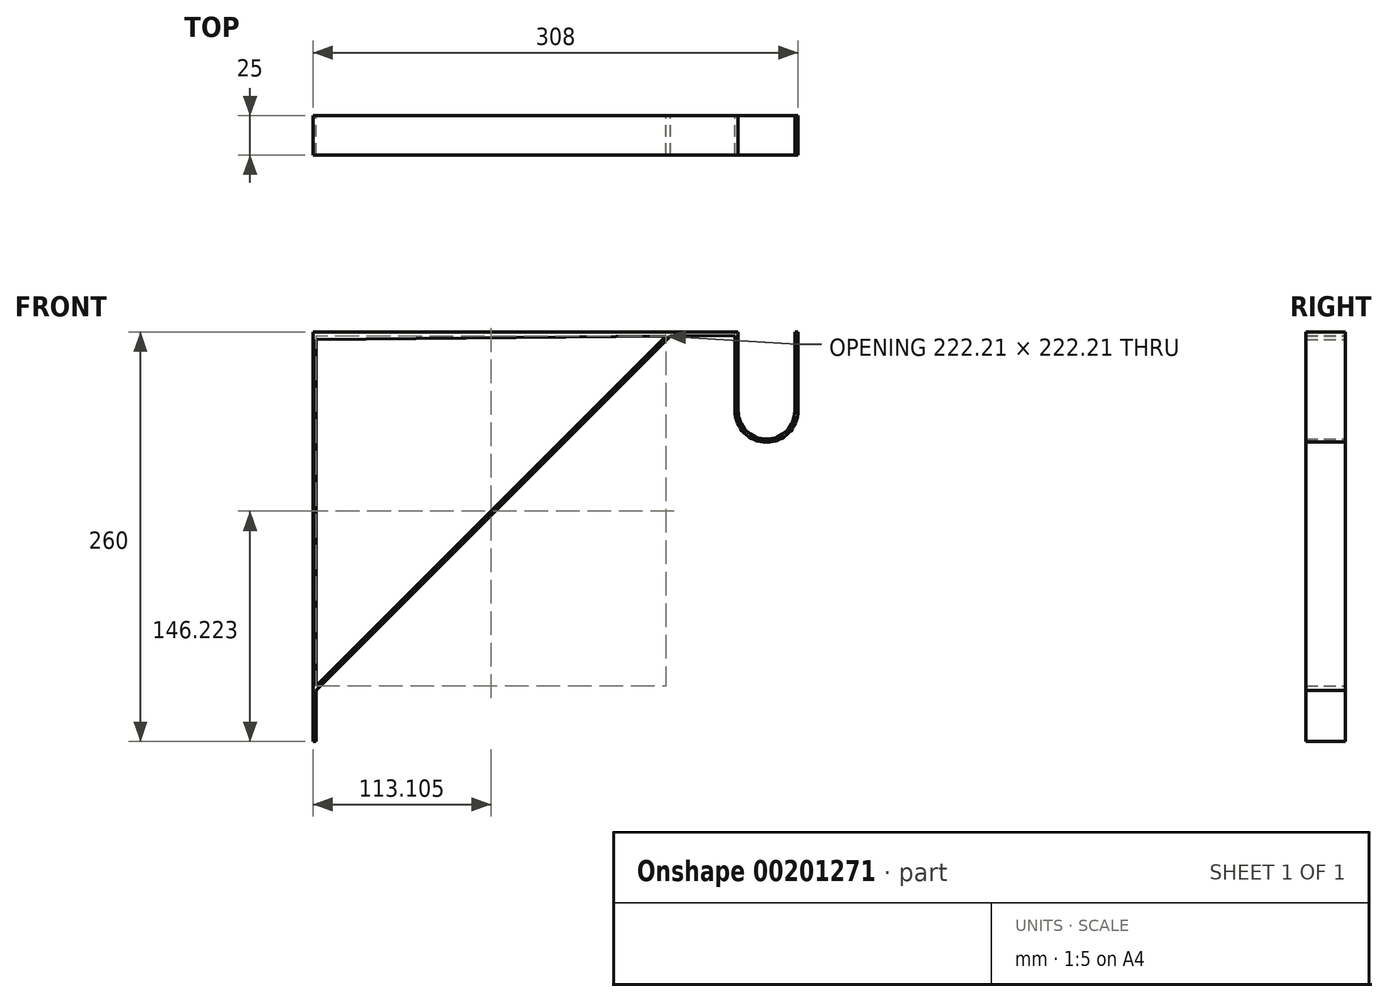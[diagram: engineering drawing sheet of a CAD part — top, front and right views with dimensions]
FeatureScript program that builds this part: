
annotation { "Feature Type Name" : "Feature", "Feature Type Description" : "" }
export const myFeature = defineFeature(function(context is Context, id is Id, definition is map)
    precondition{}
    {
        {
            var Q0;
            Q0=qCreatedBy(makeId("Front.planeOp"),FACE);
            var sketch = newSketch(context, id + "F0", { "sketchPlane" : qUnion([Q0])});
            skLineSegment(sketch, "E0", {"start": v(0, 0) * mm, "end": v(0, 260) * mm});
            skLineSegment(sketch, "E1", {"start": v(0, 260) * mm, "end": v(270, 260) * mm});
            skLineSegment(sketch, "E2", {"start": v(268, 257.76) * mm, "end": v(227.07, 257.36) * mm});
            skLineSegment(sketch, "E3", {"start": v(2, 255.13) * mm, "end": v(2, 35.12) * mm});
            skLineSegment(sketch, "E4", {"start": v(2, 0) * mm, "end": v(0, 0) * mm});
            skLineSegment(sketch, "E5", {"start": v(270, 260) * mm, "end": v(270, 210) * mm});
            skArc(sketch, "E6", {"start": v(270, 210) * mm, "mid": v(288, 192) * mm, "end": v(306, 210) * mm});
            skLineSegment(sketch, "E7", {"start": v(306, 210) * mm, "end": v(306, 260) * mm});
            skLineSegment(sketch, "E8.0", {"start": v(268, 257.76) * mm, "end": v(268, 210) * mm});
            skLineSegment(sketch, "E9.0", {"start": v(308, 210) * mm, "end": v(308, 260) * mm});
            skArc(sketch, "E9.1", {"start": v(268, 210) * mm, "mid": v(288, 190) * mm, "end": v(308, 210) * mm});
            skLineSegment(sketch, "E10", {"start": v(306, 260) * mm, "end": v(308, 260) * mm});
            skLineSegment(sketch, "E11", {"start": v(2, 35.12) * mm, "end": v(224.2, 257.33) * mm});
            skLineSegment(sketch, "E12.0", {"start": v(2, 32.29) * mm, "end": v(227.07, 257.36) * mm});
            skLineSegment(sketch, "E13.trimOffspring", {"start": v(224.2, 257.33) * mm, "end": v(2, 255.13) * mm});
            skLineSegment(sketch, "E14.trimOffspring", {"start": v(2, 32.29) * mm, "end": v(2, 0) * mm});
            skSolve(sketch);
        }
        {
            var Q0;
            Q0=makeQuery(id+"F0.imprint","IMPRINT",FACE,{"disambiguationData":[TD([[makeQuery(id+"F0.imprint","IMPRINT",EDGE,{"derivedFrom":sQuery(id+"F0.wireOp",EDGE,"E0")}),-1.0]])]});
            extrude(context, id + "F1", {"entities" : qUnion([Q0]), "depth" : 25 * mm});
        }
    });
